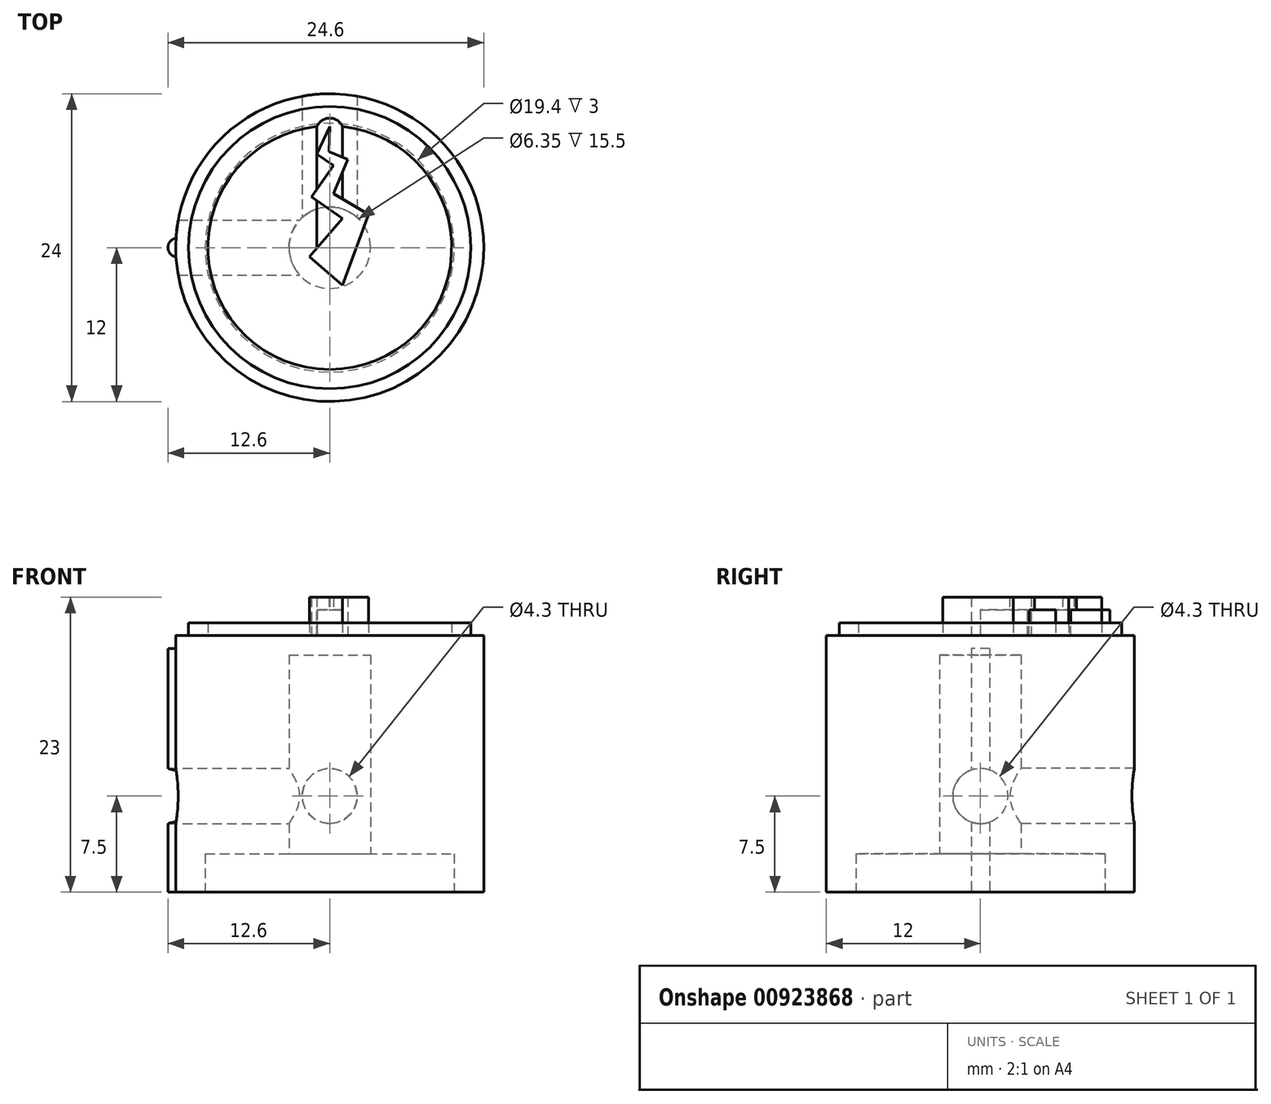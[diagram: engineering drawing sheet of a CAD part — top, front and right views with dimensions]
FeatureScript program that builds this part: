
annotation { "Feature Type Name" : "Feature", "Feature Type Description" : "" }
export const myFeature = defineFeature(function(context is Context, id is Id, definition is map)
    precondition{}
    {
        {
            var Q0;
            Q0=qCreatedBy(makeId("Top.planeOp"),FACE);
            var sketch = newSketch(context, id + "F0", { "sketchPlane" : qUnion([Q0])});
            skCircle(sketch, "E0", {"center": v(0, 0) * mm, "radius": 12 * mm});
            skSolve(sketch);
        }
        {
            var Q0;
            Q0=qSketchRegion(id+"F0",true);
            extrude(context, id + "F1", {"entities" : qUnion([Q0]), "depth" : 20 * mm, "offsetDistance" : 25 * mm});
        }
        {
            var Q0;
            Q0=makeQuery(id+"F1.opExtrude","CAP_FACE",FACE,{"disambiguationData":[OSD([sQuery(id+"F0.wireOp",EDGE,"E0")])],"isStart":true});
            var sketch = newSketch(context, id + "F2", { "sketchPlane" : qUnion([Q0])});
            skCircle(sketch, "E1", {"center": v(0, 0) * mm, "radius": 9.7 * mm});
            skLineSegment(sketch, "E2", {"start": v(0, 9.7) * mm, "end": v(0, 12) * mm, "construction": true});
            skSolve(sketch);
        }
        {
            var Q0;
            Q0=qSketchRegion(id+"F2",true);
            extrude(context, id + "F3", {"entities" : qUnion([Q0]), "operationType" : NewBodyOperationType.REMOVE, "oppositeDirection" : true, "depth" : 3 * mm, "offsetDistance" : 25 * mm});
        }
        {
            var Q0;
            Q0=makeQuery(id+"F3.boolean.opBoolean","COPY",FACE,{"derivedFrom":makeQuery(id+"F3.opExtrude","CAP_FACE",FACE,{"disambiguationData":[OSD([sQuery(id+"F2.wireOp",EDGE,"E1")])],"isStart":false})});
            var sketch = newSketch(context, id + "F4", { "sketchPlane" : qUnion([Q0])});
            skCircle(sketch, "E3", {"center": v(0, 0) * mm, "radius": 3.17 * mm});
            skSolve(sketch);
        }
        {
            var Q0;
            Q0=qSketchRegion(id+"F4",true);
            extrude(context, id + "F5", {"entities" : qUnion([Q0]), "operationType" : NewBodyOperationType.REMOVE, "oppositeDirection" : true, "depth" : 15.5 * mm, "offsetDistance" : 25 * mm});
        }
        {
            var Q0;
            Q0=qCreatedBy(makeId("Front.planeOp"),FACE);
            var sketch = newSketch(context, id + "F6", { "sketchPlane" : qUnion([Q0])});
            skCircle(sketch, "E4", {"center": v(0, 7.5) * mm, "radius": 2.15 * mm});
            skLineSegment(sketch, "E5", {"start": v(0, 0) * mm, "end": v(0, 7.5) * mm, "construction": true});
            skPoint(sketch, "E6.orphan", {"position": v(0, 15) * mm});
            skSolve(sketch);
        }
        {
            var Q0;
            Q0=qCreatedBy(makeId("Right.planeOp"),FACE);
            var sketch = newSketch(context, id + "F7", { "sketchPlane" : qUnion([Q0])});
            skCircle(sketch, "E7", {"center": v(0, 7.5) * mm, "radius": 2.15 * mm});
            skLineSegment(sketch, "E8", {"start": v(0, 0) * mm, "end": v(0, 7.5) * mm, "construction": true});
            skSolve(sketch);
        }
        {
            var Q0;
            Q0=makeQuery(id+"F1.opExtrude","CAP_FACE",FACE,{"disambiguationData":[OSD([sQuery(id+"F0.wireOp",EDGE,"E0")])],"isStart":false});
            var sketch = newSketch(context, id + "F8", { "sketchPlane" : qUnion([Q0])});
            skCircle(sketch, "E9", {"center": v(0, 0) * mm, "radius": 11 * mm});
            skCircle(sketch, "E10", {"center": v(0, 0) * mm, "radius": 9.5 * mm});
            skLineSegment(sketch, "E11", {"start": v(-11, 0) * mm, "end": v(-9.5, 0) * mm, "construction": true});
            skLineSegment(sketch, "E12", {"start": v(-12, 0) * mm, "end": v(-11, 0) * mm, "construction": true});
            skSolve(sketch);
        }
        {
            var Q0;
            Q0=makeQuery(id+"F8.imprint","IMPRINT",FACE,{"disambiguationData":[TD([[makeQuery(id+"F8.imprint","IMPRINT",EDGE,{"derivedFrom":sQuery(id+"F8.wireOp",EDGE,"E9")}),1.0]])]});
            extrude(context, id + "F9", {"entities" : qUnion([Q0]), "operationType" : NewBodyOperationType.ADD, "depth" : 1 * mm, "offsetDistance" : 25 * mm});
        }
        {
            var Q0;
            Q0=makeQuery(id+"F9.boolean.opBoolean","SPLIT",FACE,{"disambiguationData":[TD([makeQuery(id+"F9.opExtrude","SWEPT_FACE",FACE,{"disambiguationData":[OSD([sQuery(id+"F8.wireOp",EDGE,"E10")])]})])],"derivedFrom":makeQuery(id+"F1.opExtrude","CAP_FACE",FACE,{"disambiguationData":[OSD([sQuery(id+"F0.wireOp",EDGE,"E0")])],"isStart":false})});
            var sketch = newSketch(context, id + "F10", { "sketchPlane" : qUnion([Q0])});
            skLineSegment(sketch, "E13", {"start": v(-1, 0) * mm, "end": v(0, 0) * mm});
            skLineSegment(sketch, "E14", {"start": v(0, 0) * mm, "end": v(1, 0) * mm});
            skLineSegment(sketch, "E15", {"start": v(1, 0) * mm, "end": v(1, 9.45) * mm});
            skLineSegment(sketch, "E16", {"start": v(-1, 9.45) * mm, "end": v(-1, 0) * mm});
            skArc(sketch, "E17", {"start": v(1, 9.45) * mm, "mid": v(0, 10.1) * mm, "end": v(-1, 9.45) * mm});
            skSolve(sketch);
        }
        {
            var Q0;
            Q0=qSketchRegion(id+"F10",true);
            extrude(context, id + "F11", {"entities" : qUnion([Q0]), "operationType" : NewBodyOperationType.ADD, "depth" : 2 * mm, "offsetDistance" : 25 * mm});
        }
        {
            var Q0;
            Q0=qCreatedBy(makeId("Top.planeOp"),FACE);
            var sketch = newSketch(context, id + "F12", { "sketchPlane" : qUnion([Q0])});
            skArc(sketch, "E18", {"start": v(-11.97, 0.74) * mm, "mid": v(-12.6, 0) * mm, "end": v(-11.97, -0.72) * mm});
            skLineSegment(sketch, "E19", {"start": v(-11.97, 0.74) * mm, "end": v(-11.97, -0.72) * mm});
            skSolve(sketch);
        }
        {
            var Q0;
            Q0=qSketchRegion(id+"F12",true);
            var Q1;
            {var subQ0=sQuery(id+"F0.wireOp",EDGE,"E0");Q1=makeQuery(id+"F9.boolean.opBoolean","SPLIT",FACE,{"disambiguationData":[TD([makeQuery(id+"F1.opExtrude","SWEPT_FACE",FACE,{"disambiguationData":[OSD([subQ0])]})])],"derivedFrom":makeQuery(id+"F1.opExtrude","CAP_FACE",FACE,{"disambiguationData":[OSD([subQ0])],"isStart":false})});}
            extrude(context, id + "F13", {"entities" : qUnion([Q0]), "operationType" : NewBodyOperationType.ADD, "endBound" : BoundingType.UP_TO_SURFACE, "depth" : 25 * mm, "endBoundEntityFace" : qUnion([Q1]), "hasOffset" : true, "offsetDistance" : 1 * mm});
        }
        {
            var Q0;
            Q0=qSketchRegion(id+"F7",true);
            extrude(context, id + "F14", {"entities" : qUnion([Q0]), "operationType" : NewBodyOperationType.REMOVE, "oppositeDirection" : true, "depth" : 25 * mm, "offsetDistance" : 25 * mm});
        }
        {
            var Q0;
            Q0=qSketchRegion(id+"F6",true);
            extrude(context, id + "F15", {"entities" : qUnion([Q0]), "operationType" : NewBodyOperationType.REMOVE, "oppositeDirection" : true, "depth" : 25 * mm, "offsetDistance" : 25 * mm});
        }
        {
            var Q0;
            Q0=makeQuery(id+"F1.opExtrude","SWEPT_BODY",BODY,{"disambiguationData":[OSD([sQuery(id+"F0.wireOp",EDGE,"E0")])]});
            transform(context, id + "F16", {"entities" : qUnion([Q0]), "transformType" : TransformType.TRANSLATION_3D, "dx" : 40 * mm, "dy" : 0 * mm, "dz" : 0 * mm, "makeCopy" : true});
        }
        {
            var Q0;
            Q0=makeQuery(id+"F16.opPattern","COPY",FACE,{"derivedFrom":makeQuery(id+"F9.boolean.opBoolean","SPLIT",FACE,{"disambiguationData":[TD([makeQuery(id+"F9.opExtrude","SWEPT_FACE",FACE,{"disambiguationData":[OSD([sQuery(id+"F8.wireOp",EDGE,"E10")])]})])],"derivedFrom":makeQuery(id+"F1.opExtrude","CAP_FACE",FACE,{"disambiguationData":[OSD([sQuery(id+"F0.wireOp",EDGE,"E0")])],"isStart":false})}),"instanceName":"1"});
            var sketch = newSketch(context, id + "F17", { "sketchPlane" : qUnion([Q0])});
            skLineSegment(sketch, "E20", {"start": v(39, 9.45) * mm, "end": v(41, 9.45) * mm, "construction": true});
            skLineSegment(sketch, "E21", {"start": v(40, 9.45) * mm, "end": v(39, 7.3) * mm});
            skLineSegment(sketch, "E22", {"start": v(39, 7.3) * mm, "end": v(40.3, 6.41) * mm});
            skLineSegment(sketch, "E23", {"start": v(40.3, 6.41) * mm, "end": v(38.6, 3.95) * mm});
            skLineSegment(sketch, "E24", {"start": v(38.6, 3.95) * mm, "end": v(41, 2.29) * mm});
            skLineSegment(sketch, "E25", {"start": v(41, 2.29) * mm, "end": v(38.41, -0.7) * mm});
            skLineSegment(sketch, "E26", {"start": v(38.41, -0.7) * mm, "end": v(41, -2.94) * mm});
            skLineSegment(sketch, "E27", {"start": v(41, -2.94) * mm, "end": v(43.01, 2.58) * mm});
            skLineSegment(sketch, "E28", {"start": v(43.01, 2.58) * mm, "end": v(40.3, 4.21) * mm});
            skLineSegment(sketch, "E29", {"start": v(40.3, 4.21) * mm, "end": v(41.42, 6.87) * mm});
            skLineSegment(sketch, "E30", {"start": v(41.42, 6.87) * mm, "end": v(39.94, 7.5) * mm});
            skLineSegment(sketch, "E31", {"start": v(39.94, 7.5) * mm, "end": v(40, 9.45) * mm});
            skSolve(sketch);
        }
        {
            var Q0;
            Q0=qSketchRegion(id+"F17",true);
            extrude(context, id + "F18", {"entities" : qUnion([Q0]), "operationType" : NewBodyOperationType.ADD, "depth" : 3 * mm, "offsetDistance" : 25 * mm});
        }
        {
            var Q0;
            Q0=makeQuery(id+"F1.opExtrude","SWEPT_BODY",BODY,{"disambiguationData":[OSD([sQuery(id+"F0.wireOp",EDGE,"E0")])]});
            deleteBodies(context, id + "F19", {"entities" : qUnion([Q0])});
        }
    });
